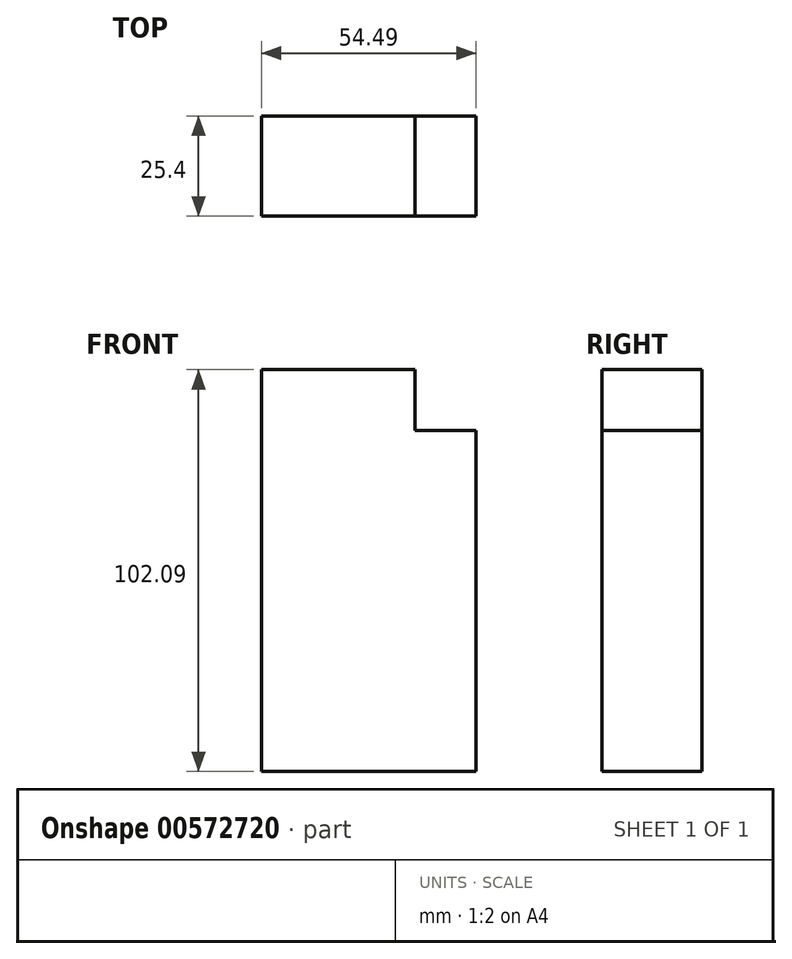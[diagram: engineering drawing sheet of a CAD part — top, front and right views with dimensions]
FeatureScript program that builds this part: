
annotation { "Feature Type Name" : "Feature", "Feature Type Description" : "" }
export const myFeature = defineFeature(function(context is Context, id is Id, definition is map)
    precondition{}
    {
        {
            var Q0;
            Q0=qCreatedBy(makeId("Front.planeOp"),FACE);
            var sketch = newSketch(context, id + "F0", { "sketchPlane" : qUnion([Q0])});
            skLineSegment(sketch, "E0.bottom", {"start": v(-21.38, -51.39) * mm, "end": v(0, -51.39) * mm});
            skLineSegment(sketch, "E0.top", {"start": v(-21.38, 50.7) * mm, "end": v(0, 50.7) * mm});
            skLineSegment(sketch, "E0.left", {"start": v(-21.38, -51.39) * mm, "end": v(-21.38, 50.7) * mm});
            skLineSegment(sketch, "E0.right", {"start": v(0, -51.39) * mm, "end": v(0, 50.7) * mm});
            skLineSegment(sketch, "E1.bottom", {"start": v(0, 50.7) * mm, "end": v(17.59, 50.7) * mm});
            skLineSegment(sketch, "E1.top", {"start": v(0, -51.39) * mm, "end": v(17.59, -51.39) * mm});
            skLineSegment(sketch, "E1.left", {"start": v(0, 50.7) * mm, "end": v(0, -51.39) * mm});
            skLineSegment(sketch, "E1.right", {"start": v(17.59, 50.7) * mm, "end": v(17.59, -51.39) * mm});
            skLineSegment(sketch, "E2.bottom", {"start": v(17.59, -51.39) * mm, "end": v(33.1, -51.39) * mm});
            skLineSegment(sketch, "E2.top", {"start": v(17.59, 35.18) * mm, "end": v(33.1, 35.18) * mm});
            skLineSegment(sketch, "E2.left", {"start": v(17.59, -51.39) * mm, "end": v(17.59, 35.18) * mm});
            skLineSegment(sketch, "E2.right", {"start": v(33.1, -51.39) * mm, "end": v(33.1, 35.18) * mm});
            skSolve(sketch);
        }
        {
            var Q0;
            Q0=makeQuery(id+"F0.imprint","IMPRINT",FACE,{"disambiguationData":[TD([[makeQuery(id+"F0.imprint","IMPRINT",EDGE,{"derivedFrom":sQuery(id+"F0.wireOp",EDGE,"E0.bottom")}),1.0]])]});
            var Q1;
            Q1=makeQuery(id+"F0.imprint","IMPRINT",FACE,{"disambiguationData":[TD([[makeQuery(id+"F0.imprint","IMPRINT",EDGE,{"derivedFrom":sQuery(id+"F0.wireOp",EDGE,"E1.bottom")}),-1.0]])]});
            var Q2;
            Q2=makeQuery(id+"F0.imprint","IMPRINT",FACE,{"disambiguationData":[TD([[makeQuery(id+"F0.imprint","IMPRINT",EDGE,{"derivedFrom":sQuery(id+"F0.wireOp",EDGE,"E2.bottom")}),1.0]])]});
            extrude(context, id + "F1", {"entities" : qUnion([Q0, Q1, Q2]), "depth" : 25.4 * mm, "offsetDistance" : 25.4 * mm});
        }
    });
